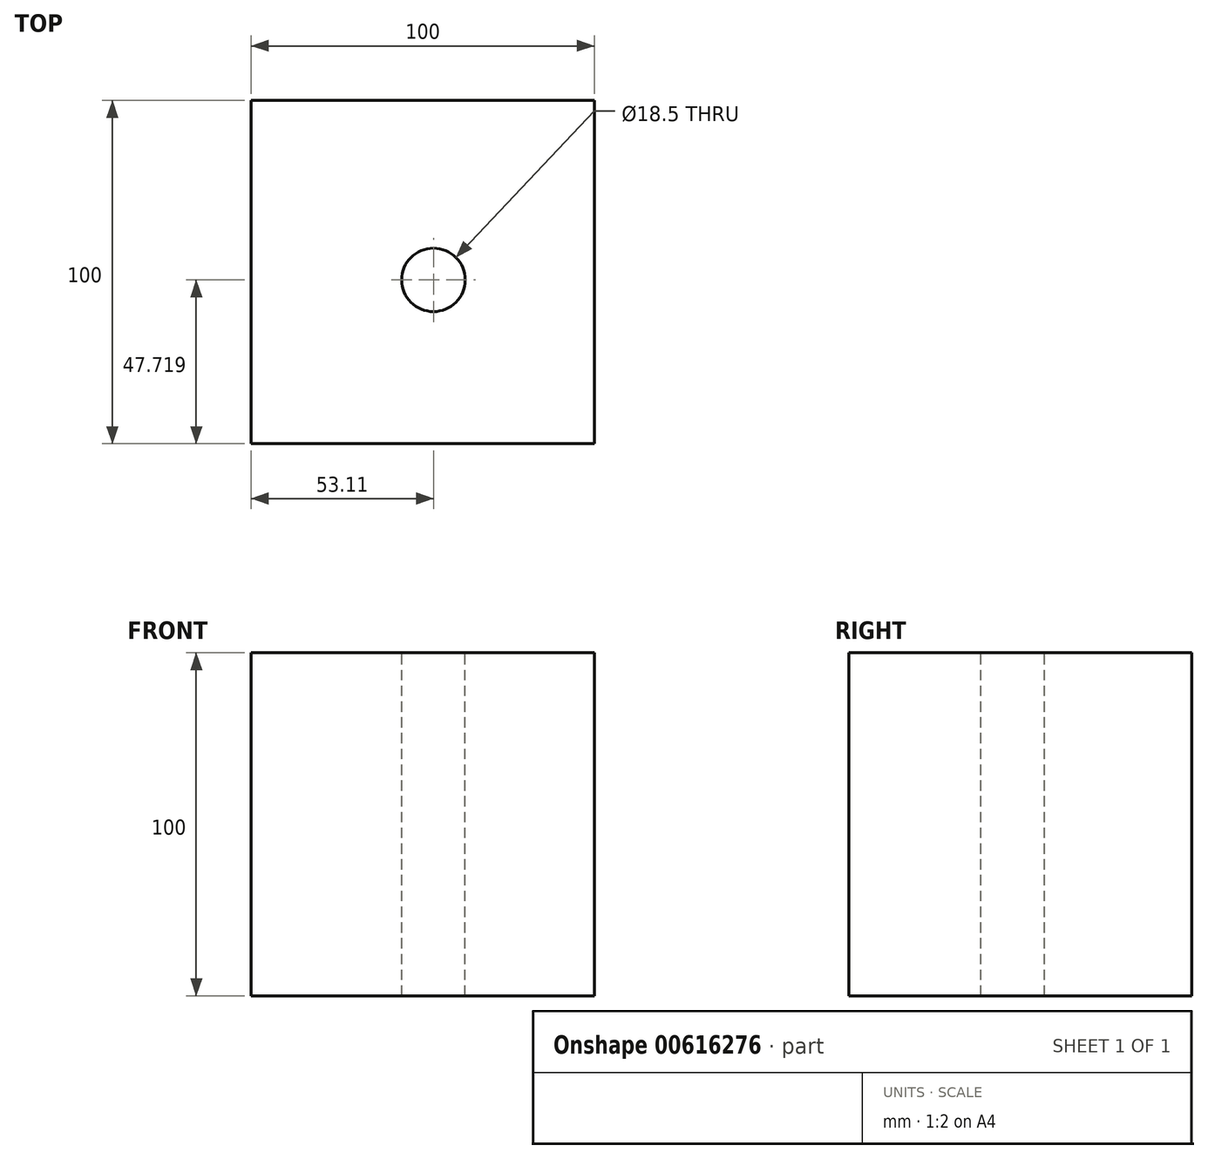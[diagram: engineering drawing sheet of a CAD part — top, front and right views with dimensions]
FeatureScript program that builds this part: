
annotation { "Feature Type Name" : "Feature", "Feature Type Description" : "" }
export const myFeature = defineFeature(function(context is Context, id is Id, definition is map)
    precondition{}
    {
        {
            var Q0;
            Q0=qCreatedBy(makeId("Front.planeOp"),FACE);
            var sketch = newSketch(context, id + "F0", { "sketchPlane" : qUnion([Q0])});
            skLineSegment(sketch, "E0.bottom", {"start": v(0, 0) * mm, "end": v(100, 0) * mm});
            skLineSegment(sketch, "E0.top", {"start": v(0, 100) * mm, "end": v(100, 100) * mm});
            skLineSegment(sketch, "E0.left", {"start": v(0, 0) * mm, "end": v(0, 100) * mm});
            skLineSegment(sketch, "E0.right", {"start": v(100, 0) * mm, "end": v(100, 100) * mm});
            skSolve(sketch);
        }
        {
            var Q0;
            Q0 = qSketchRegion(id + "F0", true);
            extrude(context, id + "F1", {"entities" : qUnion([Q0]), "depth" : 100 * mm, "offsetDistance" : 25 * mm});
        }
        {
            var Q0;
            Q0=makeQuery(id+"F1.opExtrude","SWEPT_FACE",FACE,{"disambiguationData":[OSD([sQuery(id+"F0.wireOp",EDGE,"E0.top")])]});
            var sketch = newSketch(context, id + "F2", { "sketchPlane" : qUnion([Q0])});
            skPoint(sketch, "E1", {"position": v(53.1, -52.28) * mm});
            skSolve(sketch);
        }
        {
            var Q0;
            Q0=sQuery(id+"F2.wireOp",VERTEX,"E1");
            var Q1;
            Q1=makeQuery(id+"F1.opExtrude","SWEPT_BODY",BODY,{"disambiguationData":[OSD([sQuery(id+"F0.wireOp",EDGE,"E0.bottom"),sQuery(id+"F0.wireOp",EDGE,"E0.top"),sQuery(id+"F0.wireOp",EDGE,"E0.left"),sQuery(id+"F0.wireOp",EDGE,"E0.right")])]});
            hole(context, id + "F3", {"style" : HoleStyle.SIMPLE, "endStyle" : HoleEndStyle.THROUGH, "standardTappedOrClearance" : lookupTablePath({ "standard" : "ISO", "engagement" : "75%", "pitch" : "1.5 mm", "size" : "M20", "type" : "Tapped" }), "standardBlindInLast" : lookupTablePath({ "standard" : "ISO", "engagement" : "75%", "pitch" : "1.5 mm", "size" : "M20", "type" : "Tapped" }), "holeDiameter" : 18.5 * mm, "majorDiameter" : 20 * mm, "showTappedDepth" : true, "isTappedThrough" : true, "tappedDepth" : 12 * mm, "tapClearance" : 3, "locations" : qUnion([Q0]), "scope" : qUnion([Q1])});
        }
    });
